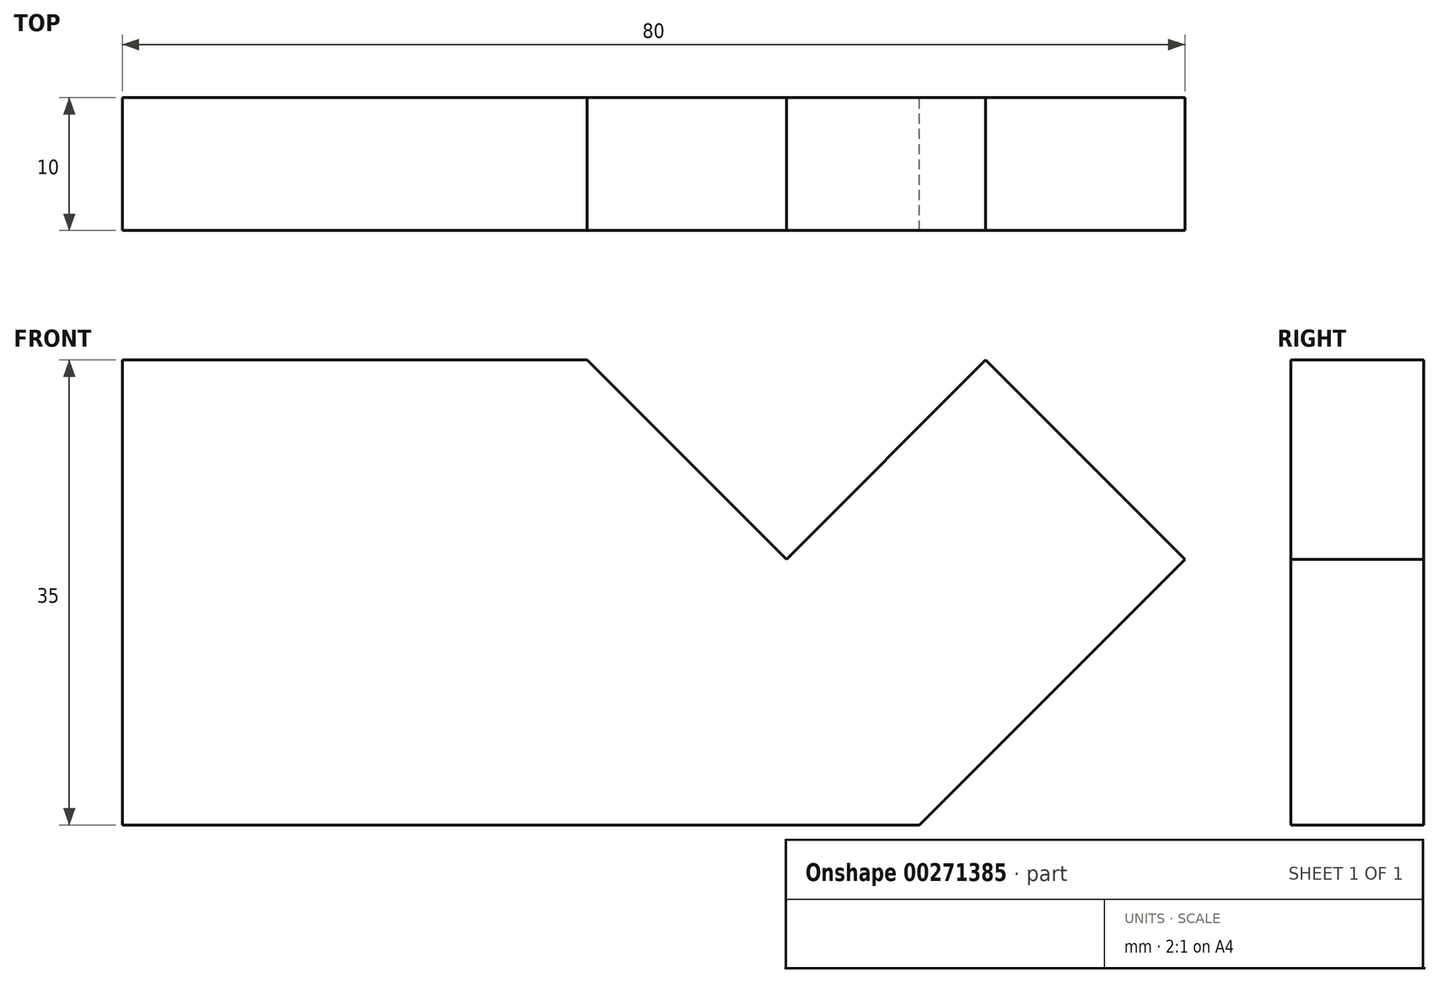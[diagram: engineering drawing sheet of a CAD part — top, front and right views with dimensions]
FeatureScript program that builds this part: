
annotation { "Feature Type Name" : "Feature", "Feature Type Description" : "" }
export const myFeature = defineFeature(function(context is Context, id is Id, definition is map)
    precondition{}
    {
        {
            var Q0;
            Q0=qCreatedBy(makeId("Front.planeOp"),FACE);
            var sketch = newSketch(context, id + "F0", { "sketchPlane" : qUnion([Q0])});
            skLineSegment(sketch, "E0", {"start": v(0, 0) * mm, "end": v(0, 35) * mm});
            skLineSegment(sketch, "E1", {"start": v(0, 35) * mm, "end": v(35, 35) * mm});
            skLineSegment(sketch, "E2", {"start": v(0, 0) * mm, "end": v(60, 0) * mm});
            skLineSegment(sketch, "E3", {"start": v(35, 35) * mm, "end": v(50, 20) * mm});
            skLineSegment(sketch, "E4", {"start": v(50, 20) * mm, "end": v(65, 35) * mm});
            skLineSegment(sketch, "E5", {"start": v(65, 35) * mm, "end": v(80, 20) * mm});
            skLineSegment(sketch, "E6", {"start": v(80, 20) * mm, "end": v(60, 0) * mm});
            skSolve(sketch);
        }
        {
            var Q0;
            Q0 = qSketchRegion(id + "F0", true);
            extrude(context, id + "F1", {"entities" : qUnion([Q0]), "depth" : 10 * mm});
        }
    });
